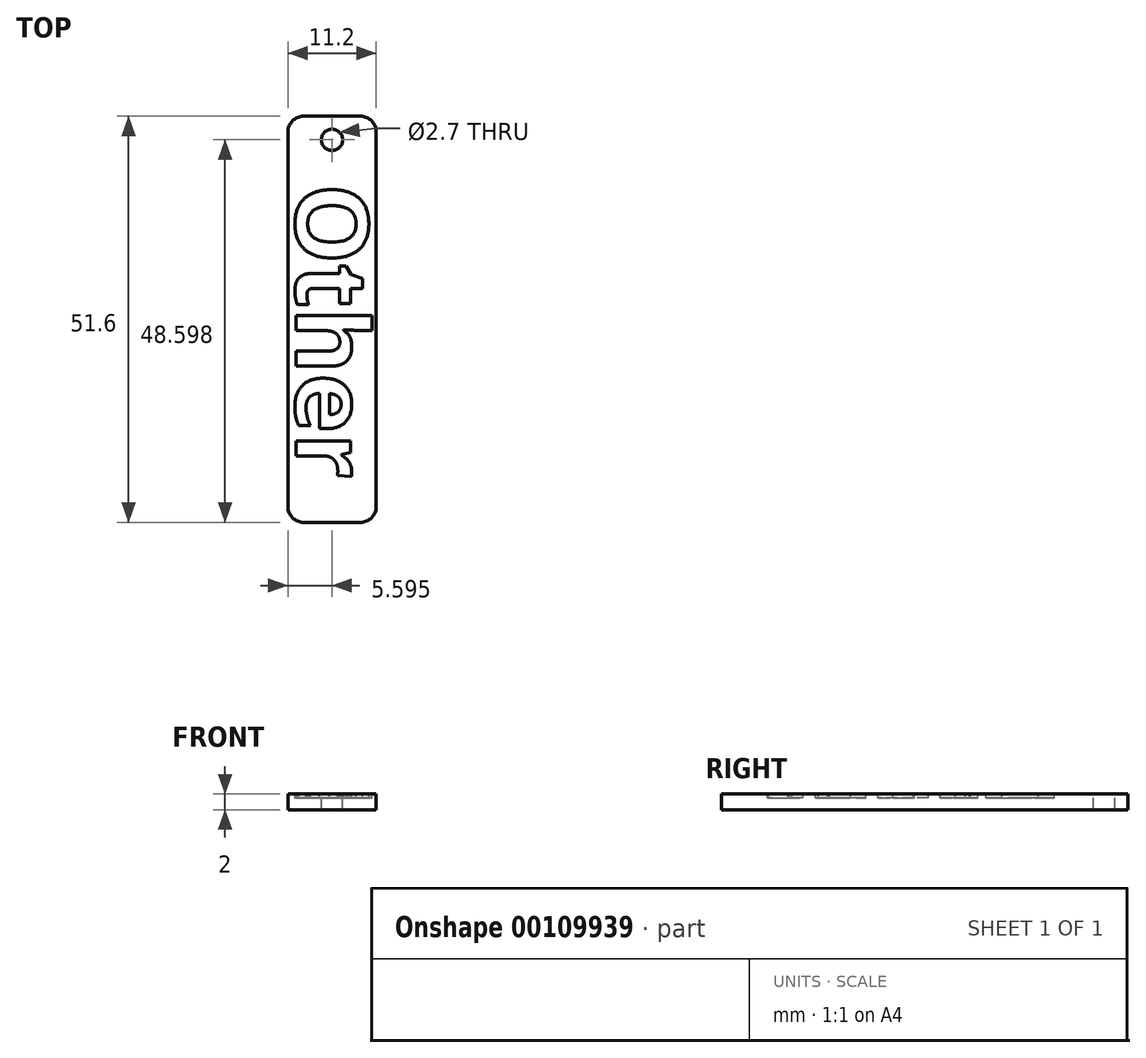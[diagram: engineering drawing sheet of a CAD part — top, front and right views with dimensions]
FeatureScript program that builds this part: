
annotation { "Feature Type Name" : "Feature", "Feature Type Description" : "" }
export const myFeature = defineFeature(function(context is Context, id is Id, definition is map)
    precondition{}
    {
        {
            var Q0;
            Q0=qCreatedBy(makeId("Top.planeOp"),FACE);
            var sketch = newSketch(context, id + "F0", { "sketchPlane" : qUnion([Q0])});
            skLineSegment(sketch, "E0.bottom", {"start": v(-49.26, 73.73) * mm, "end": v(-38.06, 73.73) * mm});
            skLineSegment(sketch, "E0.top", {"start": v(-49.26, 22.13) * mm, "end": v(-38.06, 22.13) * mm});
            skLineSegment(sketch, "E0.left", {"start": v(-49.26, 73.73) * mm, "end": v(-49.26, 22.13) * mm});
            skLineSegment(sketch, "E0.right", {"start": v(-38.06, 73.73) * mm, "end": v(-38.06, 22.13) * mm});
            skCircle(sketch, "E1", {"center": v(-43.66, 70.73) * mm, "radius": 1.35 * mm});
            skText(sketch, "E2", { "text": "Other", "fontName": "OpenSans-Bold.ttf"});
            const initialGuessF0  = {"E2": [-0.04826, 0.06514, 0, -1, 0.0092]};
            skSetInitialGuess(sketch, initialGuessF0);
            skSolve(sketch);
        }
        {
            var Q0;
            Q0=makeQuery(id+"F0.imprint","IMPRINT",FACE,{"disambiguationData":[TD([[makeQuery(id+"F0.imprint","IMPRINT",EDGE,{"derivedFrom":sQuery(id+"F0.wireOp",EDGE,"E2.sketch_text.stroke-8")}),1.0]])]});
            var Q1;
            Q1=makeQuery(id+"F0.imprint","IMPRINT",FACE,{"disambiguationData":[TD([[makeQuery(id+"F0.imprint","IMPRINT",EDGE,{"derivedFrom":sQuery(id+"F0.wireOp",EDGE,"E2.sketch_text.stroke-14")}),-1.0]])]});
            var Q2;
            Q2=makeQuery(id+"F0.imprint","IMPRINT",FACE,{"disambiguationData":[TD([[makeQuery(id+"F0.imprint","IMPRINT",EDGE,{"derivedFrom":sQuery(id+"F0.wireOp",EDGE,"E2.sketch_text.stroke-32")}),-1.0]])]});
            var Q3;
            Q3=makeQuery(id+"F0.imprint","IMPRINT",FACE,{"disambiguationData":[TD([[makeQuery(id+"F0.imprint","IMPRINT",EDGE,{"derivedFrom":sQuery(id+"F0.wireOp",EDGE,"E2.sketch_text.stroke-49")}),-1.0]])]});
            var Q4;
            Q4=makeQuery(id+"F0.imprint","IMPRINT",FACE,{"disambiguationData":[TD([[makeQuery(id+"F0.imprint","IMPRINT",EDGE,{"derivedFrom":sQuery(id+"F0.wireOp",EDGE,"E2.sketch_text.stroke-69")}),-1.0]])]});
            var Q5;
            Q5=makeQuery(id+"F0.imprint","IMPRINT",FACE,{"disambiguationData":[TD([[makeQuery(id+"F0.imprint","IMPRINT",EDGE,{"derivedFrom":sQuery(id+"F0.wireOp",EDGE,"E0.bottom")}),-1.0]])]});
            var Q6;
            Q6=makeQuery(id+"F0.imprint","IMPRINT",FACE,{"disambiguationData":[TD([[makeQuery(id+"F0.imprint","IMPRINT",EDGE,{"derivedFrom":sQuery(id+"F0.wireOp",EDGE,"E2.sketch_text.stroke-0")}),-1.0]])]});
            var Q7;
            Q7=makeQuery(id+"F0.imprint","IMPRINT",FACE,{"disambiguationData":[TD([[makeQuery(id+"F0.imprint","IMPRINT",EDGE,{"derivedFrom":sQuery(id+"F0.wireOp",EDGE,"E2.sketch_text.stroke-49")}),1.0]])]});
            extrude(context, id + "F1", {"entities" : qUnion([Q0, Q1, Q2, Q3, Q4, Q5, Q6, Q7]), "oppositeDirection" : true, "depth" : 2 * mm});
        }
        {
            var Q0;
            Q0=makeQuery(id+"F0.imprint","IMPRINT",FACE,{"disambiguationData":[TD([[makeQuery(id+"F0.imprint","IMPRINT",EDGE,{"derivedFrom":sQuery(id+"F0.wireOp",EDGE,"E2.sketch_text.stroke-0")}),-1.0]])]});
            var Q1;
            Q1=makeQuery(id+"F0.imprint","IMPRINT",FACE,{"disambiguationData":[TD([[makeQuery(id+"F0.imprint","IMPRINT",EDGE,{"derivedFrom":sQuery(id+"F0.wireOp",EDGE,"E2.sketch_text.stroke-16")}),-1.0]])]});
            var Q2;
            Q2=makeQuery(id+"F0.imprint","IMPRINT",FACE,{"disambiguationData":[TD([[makeQuery(id+"F0.imprint","IMPRINT",EDGE,{"derivedFrom":sQuery(id+"F0.wireOp",EDGE,"E2.sketch_text.stroke-28")}),-1.0]])]});
            var Q3;
            Q3=makeQuery(id+"F0.imprint","IMPRINT",FACE,{"disambiguationData":[TD([[makeQuery(id+"F0.imprint","IMPRINT",EDGE,{"derivedFrom":sQuery(id+"F0.wireOp",EDGE,"E2.sketch_text.stroke-36")}),-1.0]])]});
            var Q4;
            Q4=makeQuery(id+"F0.imprint","IMPRINT",FACE,{"disambiguationData":[TD([[makeQuery(id+"F0.imprint","IMPRINT",EDGE,{"derivedFrom":sQuery(id+"F0.wireOp",EDGE,"E2.sketch_text.stroke-49")}),-1.0]])]});
            var Q5;
            Q5=makeQuery(id+"F0.imprint","IMPRINT",FACE,{"disambiguationData":[TD([[makeQuery(id+"F0.imprint","IMPRINT",EDGE,{"derivedFrom":sQuery(id+"F0.wireOp",EDGE,"E2.sketch_text.stroke-69")}),-1.0]])]});
            var Q6;
            Q6=qConstructionFilter(qBodyType(qCreatedBy(id+"F0",EDGE),BodyType.WIRE),ConstructionObject.NO);
            extrude(context, id + "F2", {"entities" : qUnion([Q0, Q1, Q2, Q3, Q4, Q5]), "operationType" : NewBodyOperationType.REMOVE, "surfaceEntities" : qUnion([Q6]), "oppositeDirection" : true, "depth" : .5 * mm});
        }
        {
            var Q0;
            Q0=makeQuery(id+"F1.opExtrude","SWEPT_EDGE",EDGE,{"disambiguationData":[OSD([sQuery(id+"F0.wireOp",EDGE,"E0.bottom"),sQuery(id+"F0.wireOp",EDGE,"E0.left")])]});
            var Q1;
            Q1=makeQuery(id+"F1.opExtrude","SWEPT_EDGE",EDGE,{"disambiguationData":[OSD([sQuery(id+"F0.wireOp",EDGE,"E0.bottom"),sQuery(id+"F0.wireOp",EDGE,"E0.right")])]});
            var Q2;
            Q2=makeQuery(id+"F1.opExtrude","SWEPT_EDGE",EDGE,{"disambiguationData":[OSD([sQuery(id+"F0.wireOp",EDGE,"E0.top"),sQuery(id+"F0.wireOp",EDGE,"E0.right")])]});
            var Q3;
            Q3=makeQuery(id+"F1.opExtrude","SWEPT_EDGE",EDGE,{"disambiguationData":[OSD([sQuery(id+"F0.wireOp",EDGE,"E0.top"),sQuery(id+"F0.wireOp",EDGE,"E0.left")])]});
            fillet(context, id + "F3", {"entities" : qUnion([Q0, Q1, Q2, Q3]), "radius" : 2 * mm, "tangentPropagation" : true, "allowEdgeOverflow" : false});
        }
    });
